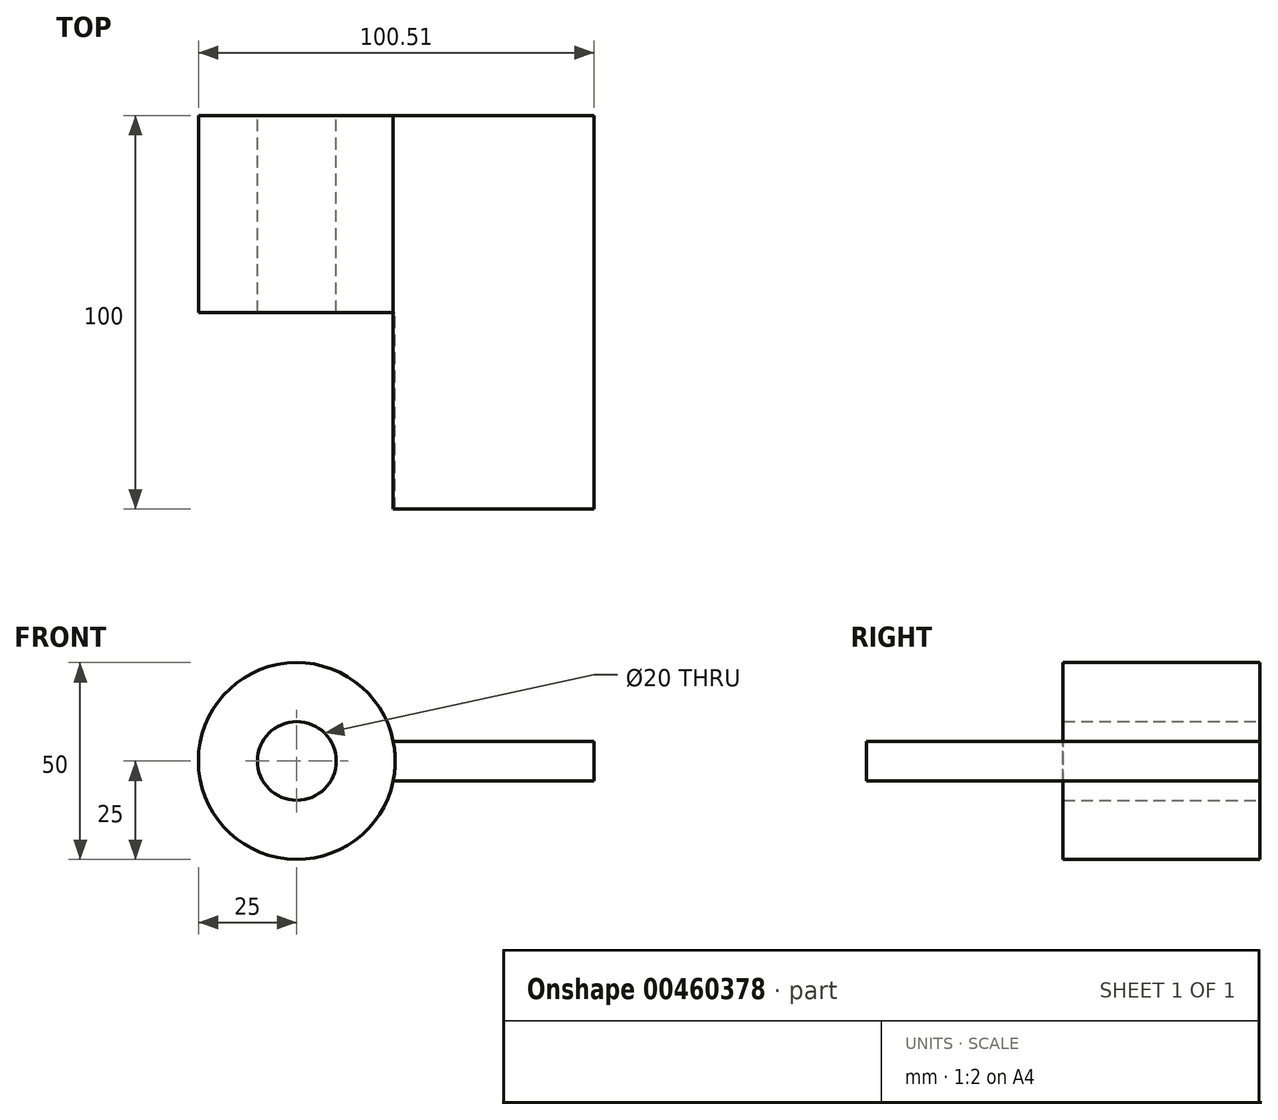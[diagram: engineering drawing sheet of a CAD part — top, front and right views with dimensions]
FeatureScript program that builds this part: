
annotation { "Feature Type Name" : "Feature", "Feature Type Description" : "" }
export const myFeature = defineFeature(function(context is Context, id is Id, definition is map)
    precondition{}
    {
        {
            var Q0;
            Q0=qCreatedBy(makeId("Front.planeOp"),FACE);
            var sketch = newSketch(context, id + "F0", { "sketchPlane" : qUnion([Q0])});
            skCircle(sketch, "E0", {"center": v(0, 0) * mm, "radius": 25 * mm});
            skCircle(sketch, "E1", {"center": v(0, 0) * mm, "radius": 10 * mm});
            skLineSegment(sketch, "E2", {"start": v(0, 0) * mm, "end": v(50, 0) * mm, "construction": true});
            skLineSegment(sketch, "E3.bottom", {"start": v(75.5, -5) * mm, "end": v(24.5, -5) * mm});
            skLineSegment(sketch, "E3.top", {"start": v(75.5, 5) * mm, "end": v(24.5, 5) * mm});
            skLineSegment(sketch, "E3.left", {"start": v(75.5, -5) * mm, "end": v(75.5, 5) * mm});
            skPoint(sketch, "E3.middle", {"position": v(50, 0) * mm});
            skSolve(sketch);
        }
        {
            var Q0;
            Q0=makeQuery(id+"F0.imprint","IMPRINT",FACE,{"disambiguationData":[TD([[makeQuery(id+"F0.imprint","IMPRINT",EDGE,{"derivedFrom":sQuery(id+"F0.wireOp",EDGE,"E1")}),-1.0]])]});
            extrude(context, id + "F1", {"entities" : qUnion([Q0]), "depth" : 50 * mm});
        }
        {
            var Q0;
            {var subQ0=sQuery(id+"F0.wireOp",EDGE,"E3.bottom");Q0=makeQuery(id+"F0.imprint","IMPRINT",FACE,{"disambiguationData":[TD([[makeQuery(id+"F0.imprint","IMPRINT",EDGE,{"derivedFrom":subQ0}),-1.0]])]});}
            extrude(context, id + "F2", {"entities" : qUnion([Q0]), "operationType" : NewBodyOperationType.ADD, "depth" : 100 * mm});
        }
    });
